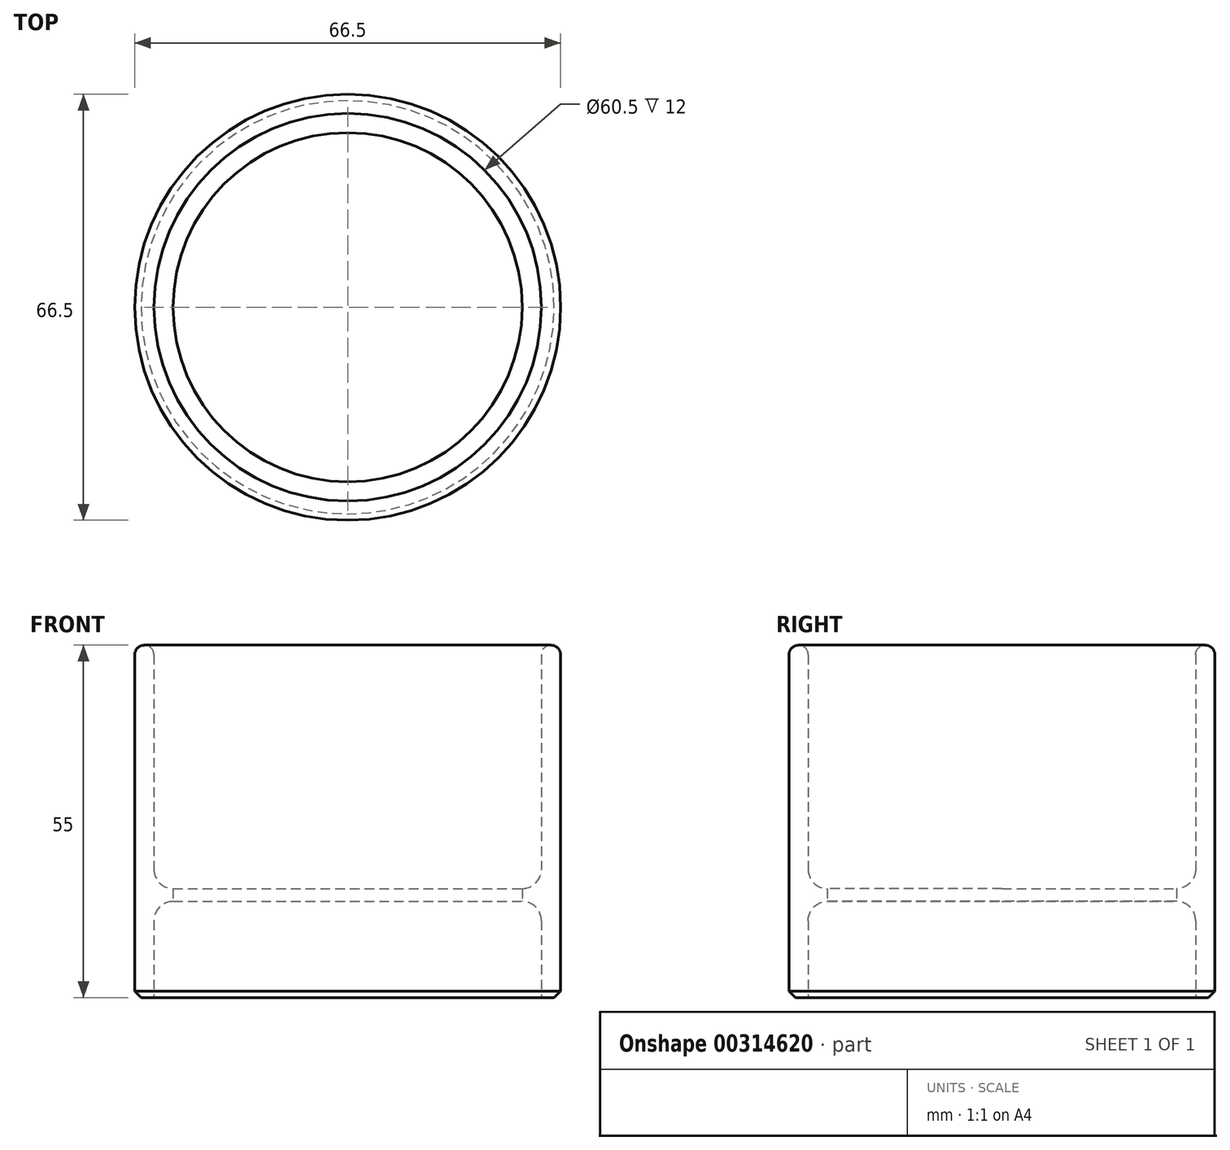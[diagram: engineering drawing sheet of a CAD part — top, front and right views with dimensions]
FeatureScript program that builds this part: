
annotation { "Feature Type Name" : "Feature", "Feature Type Description" : "" }
export const myFeature = defineFeature(function(context is Context, id is Id, definition is map)
    precondition{}
    {
        {
            var Q0;
            Q0=qCreatedBy(makeId("Front.planeOp"),FACE);
            var sketch = newSketch(context, id + "F0", { "sketchPlane" : qUnion([Q0])});
            skLineSegment(sketch, "E0", {"start": v(33.25, 0) * mm, "end": v(33.25, 55) * mm});
            skLineSegment(sketch, "E1", {"start": v(33.25, 55) * mm, "end": v(30.25, 55) * mm});
            skLineSegment(sketch, "E2", {"start": v(30.25, 55) * mm, "end": v(30.25, 17) * mm});
            skLineSegment(sketch, "E3", {"start": v(30.25, 17) * mm, "end": v(27.25, 17) * mm});
            skLineSegment(sketch, "E4", {"start": v(27.25, 17) * mm, "end": v(27.25, 15) * mm});
            skLineSegment(sketch, "E5", {"start": v(27.25, 15) * mm, "end": v(30.25, 15) * mm});
            skLineSegment(sketch, "E6", {"start": v(30.25, 15) * mm, "end": v(30.25, 0) * mm});
            skLineSegment(sketch, "E7", {"start": v(30.25, 0) * mm, "end": v(33.25, 0) * mm});
            skLineSegment(sketch, "E8", {"start": v(0, -36.92) * mm, "end": v(0, 94.7) * mm, "construction": true});
            skSolve(sketch);
        }
        {
            var Q0;
            Q0=makeQuery(id+"F0.imprint","IMPRINT",FACE,{"disambiguationData":[TD([[makeQuery(id+"F0.imprint","IMPRINT",EDGE,{"derivedFrom":sQuery(id+"F0.wireOp",EDGE,"E0")}),1.0]])]});
            var Q1;
            Q1=sQuery(id+"F0.wireOp",EDGE,"E8");
            revolve(context, id + "F1", {"entities" : qUnion([Q0]), "axis" : qUnion([Q1]), "revolveType" : RevolveType.FULL});
        }
        {
            var Q0;
            Q0=makeQuery(id+"F1.opRevolve","SWEPT_EDGE",EDGE,{"disambiguationData":[OSD([sQuery(id+"F0.wireOp",EDGE,"E2"),sQuery(id+"F0.wireOp",EDGE,"E3")])]});
            fillet(context, id + "F2", {"entities" : qUnion([Q0]), "radius" : 3 * mm, "tangentPropagation" : true, "allowEdgeOverflow" : false});
        }
        {
            var Q0;
            Q0=makeQuery(id+"F1.opRevolve","SWEPT_EDGE",EDGE,{"disambiguationData":[OSD([sQuery(id+"F0.wireOp",EDGE,"E5"),sQuery(id+"F0.wireOp",EDGE,"E6")])]});
            fillet(context, id + "F3", {"entities" : qUnion([Q0]), "radius" : 3 * mm, "tangentPropagation" : true, "allowEdgeOverflow" : false});
        }
        {
            var Q0;
            Q0=makeQuery(id+"F1.opRevolve","SWEPT_EDGE",EDGE,{"disambiguationData":[OSD([sQuery(id+"F0.wireOp",EDGE,"E1"),sQuery(id+"F0.wireOp",EDGE,"E2")])]});
            var Q1;
            Q1=makeQuery(id+"F1.opRevolve","SWEPT_EDGE",EDGE,{"disambiguationData":[OSD([sQuery(id+"F0.wireOp",EDGE,"E0"),sQuery(id+"F0.wireOp",EDGE,"E1")])]});
            fillet(context, id + "F4", {"entities" : qUnion([Q0, Q1]), "radius" : 1.5 * mm, "tangentPropagation" : true, "allowEdgeOverflow" : false});
        }
        {
            var Q0;
            Q0=makeQuery(id+"F1.opRevolve","SWEPT_EDGE",EDGE,{"disambiguationData":[OSD([sQuery(id+"F0.wireOp",EDGE,"E0"),sQuery(id+"F0.wireOp",EDGE,"E7")])]});
            chamfer(context, id + "F5", {"entities" : qUnion([Q0]), "width" : 1 * mm, "tangentPropagation" : true});
        }
    });
